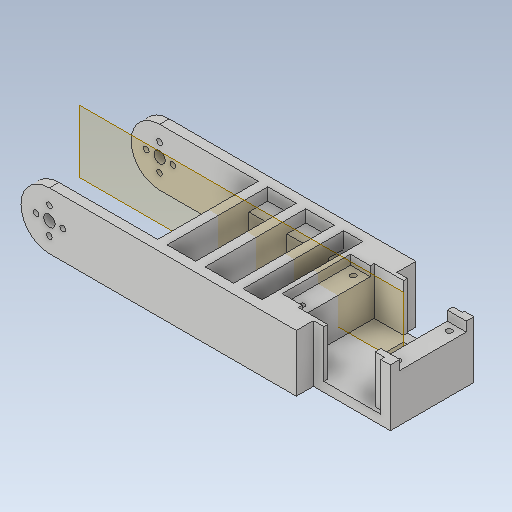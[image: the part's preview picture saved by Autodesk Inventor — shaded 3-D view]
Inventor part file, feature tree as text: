
AUTODESK INVENTOR PART (.ipt)
format: ipt  version: 2020.1 (Build 241239000, 239)  size: 380,416 bytes
history: native  units: mm
features: other x11, extrude x9, sketch x7, plane x1, mirror x1
ambient origin geometry x8: Origin, YZ Plane, XZ Plane, XY Plane, X Axis, Y Axis, Z Axis, Center Point
bodies: Solid1 (feature_tree)
feature tree (29):
  extrude  "base_leg"  Depth=6.0mm
  plane  "Work Plane1"
  mirror  "Mirror1"
  extrude  "base_servo_place"  Depth=3.0mm
  other  "servo_sketch"
  extrude  "servo_place"  Depth=40.0mm
  extrude  "beams"  Depth=5.0mm TaperAngle=0.0deg
  extrude  "servo_place_lock_holes"  Depth=30.5mm
  extrude  "Extrusion6"  Depth=40.5mm
  extrude  "Extrusion7"  Depth=40.5mm
  extrude  "Extrusión8"  Depth=40.5mm
  extrude  "Extrusión9"  Depth=23.0mm
  other  "Edición directa1"
  other  "Edición directa2"
  other  "Edición directa3"
  other  "Edición directa4"
  sketch  "Sketch1"  dims[d0=30.0mm d1=6.0mm]
  sketch  "Sketch3"  dims[d2=14.0mm d3=3.0mm]
  sketch  "Sketch4"  dims[d4=40.0mm d6=360.0deg d8=130.0mm]
  sketch  "Sketch5"  dims[d9=130.0mm d10=5.0mm d11=0.0mm]
  sketch  "Sketch6"  dims[d12=26.0mm d13=30.5mm]
  sketch  "Boceto8"  dims[d14=21.0mm d15=40.5mm]
  sketch  "Boceto9"  dims[d16=42.0mm d17=40.5mm d18=40.5mm d19=23.0mm d20=180.0deg d21=5.0mm d22=0.0mm d23=25.0mm d24=0.0mm d25=10.0mm d26=15.0mm d27=30.0mm d28=10.0mm d29=15.0mm d30=30.0mm d31=10.0mm d32=5.0mm d33=15.0mm d34=5.0mm d35=15.0mm d36=52.0mm d37=52.0mm d38=5.0mm d39=25.0mm d40=0.0mm d41=5.0mm d42=15.0mm d43=15.0mm d44=5.0mm d45=15.0mm d46=15.0mm d47=3.0mm d48=3.0mm d49=3.0mm d50=3.0mm d51=25.0mm d52=0.0mm d53=19.0mm d54=38.0mm d55=61.0mm d56=180.0deg d57=38.0mm d58=90.0deg d59=5.0mm d60=0.0mm d61=27.0mm d62=9.0mm d63=10.0mm d64=1.0mm d65=14.0mm d66=10.0mm d67=5.0mm d68=0.0mm d74=15.0mm d75=6.5mm d76=8.0mm d77=13.0mm d78=2.0mm d79=10.0mm d80=15.0mm d81=2.0mm d82=45.0mm d83=0.0mm d84=15.0mm d85=6.5mm d86=8.0mm d87=13.0mm d88=45.0mm d89=0.0mm d90=0.0mm d91=0.0mm d92=-1.0mm d93=0.0mm d94=0.0mm d95=1.0mm d96=0.0mm d97=0.0mm d98=2.0mm d99=0.0mm d100=0.0mm d101=1.0mm d102=0.0mm d103=0.0mm d104=-3.0mm d105=0.0mm d106=0.0mm d107=-3.0mm]
  other  "Desplazar1"
  other  "Desplazar2"
  other  "Desplazar3"
  other  "Desplazar4"
  other  "Desplazar5"
  other  "Desplazar6"
